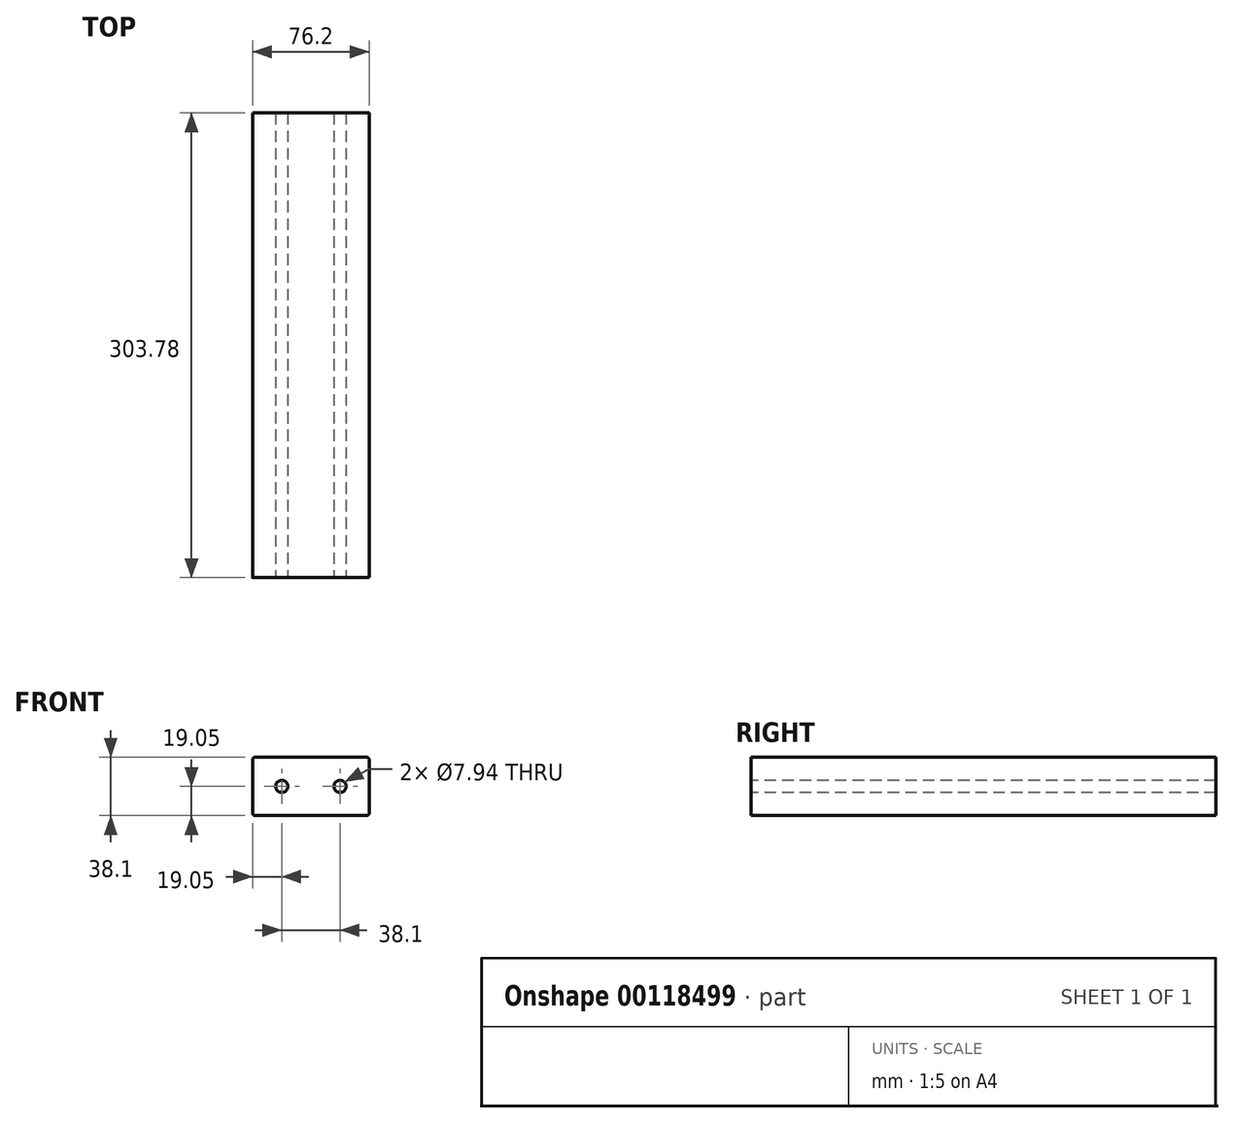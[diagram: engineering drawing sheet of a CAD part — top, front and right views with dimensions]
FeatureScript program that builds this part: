
annotation { "Feature Type Name" : "Feature", "Feature Type Description" : "" }
export const myFeature = defineFeature(function(context is Context, id is Id, definition is map)
    precondition{}
    {
        {
            var Q0;
            Q0=qCreatedBy(makeId("Front.planeOp"),FACE);
            var sketch = newSketch(context, id + "F0", { "sketchPlane" : qUnion([Q0])});
            skLineSegment(sketch, "E0.bottom", {"start": v(36.51, 19.05) * mm, "end": v(-36.51, 19.05) * mm});
            skLineSegment(sketch, "E0.top", {"start": v(36.51, -19.05) * mm, "end": v(-36.51, -19.05) * mm});
            skLineSegment(sketch, "E0.left", {"start": v(38.1, 17.46) * mm, "end": v(38.1, -17.46) * mm});
            skLineSegment(sketch, "E0.right", {"start": v(-38.1, 17.46) * mm, "end": v(-38.1, -17.46) * mm});
            skPoint(sketch, "E0.middle", {"position": v(0, 0) * mm});
            skPoint(sketch, "E1.visualSharp", {"position": v(38.1, 19.05) * mm});
            skArc(sketch, "E1.filletArc", {"start": v(38.1, 17.46) * mm, "mid": v(37.64, 18.59) * mm, "end": v(36.51, 19.05) * mm});
            skPoint(sketch, "E2.visualSharp", {"position": v(38.1, -19.05) * mm});
            skArc(sketch, "E2.filletArc", {"start": v(36.51, -19.05) * mm, "mid": v(37.64, -18.59) * mm, "end": v(38.1, -17.46) * mm});
            skPoint(sketch, "E3.visualSharp", {"position": v(-38.1, -19.05) * mm});
            skArc(sketch, "E3.filletArc", {"start": v(-38.1, -17.46) * mm, "mid": v(-37.64, -18.59) * mm, "end": v(-36.51, -19.05) * mm});
            skPoint(sketch, "E4.visualSharp", {"position": v(-38.1, 19.05) * mm});
            skArc(sketch, "E4.filletArc", {"start": v(-36.51, 19.05) * mm, "mid": v(-37.64, 18.59) * mm, "end": v(-38.1, 17.46) * mm});
            skSolve(sketch);
        }
        {
            var Q0;
            Q0=makeQuery(id+"F0.imprint","IMPRINT",FACE,{"disambiguationData":[TD([[makeQuery(id+"F0.imprint","IMPRINT",EDGE,{"derivedFrom":sQuery(id+"F0.wireOp",EDGE,"E0.bottom")}),1.0]])]});
            extrude(context, id + "F1", {"entities" : qUnion([Q0]), "depth" : 303.78 * mm, "symmetric" : true});
        }
        {
            var Q0;
            Q0=makeQuery(id+"F1.opExtrude","CAP_FACE",FACE,{"disambiguationData":[OSD([sQuery(id+"F0.wireOp",EDGE,"E0.bottom"),sQuery(id+"F0.wireOp",EDGE,"E0.top"),sQuery(id+"F0.wireOp",EDGE,"E0.left"),sQuery(id+"F0.wireOp",EDGE,"E0.right"),sQuery(id+"F0.wireOp",EDGE,"E1.filletArc"),sQuery(id+"F0.wireOp",EDGE,"E2.filletArc"),sQuery(id+"F0.wireOp",EDGE,"E3.filletArc"),sQuery(id+"F0.wireOp",EDGE,"E4.filletArc")])],"isStart":false});
            var sketch = newSketch(context, id + "F2", { "sketchPlane" : qUnion([Q0])});
            skLineSegment(sketch, "E5", {"start": v(0, 0) * mm, "end": v(19.05, 0) * mm});
            skCircle(sketch, "E6", {"center": v(19.05, 0) * mm, "radius": 3.97 * mm});
            skLineSegment(sketch, "E7", {"start": v(-19.05, 0) * mm, "end": v(0, 0) * mm});
            skCircle(sketch, "E8", {"center": v(-19.05, 0) * mm, "radius": 3.97 * mm});
            skSolve(sketch);
        }
        {
            var Q0;
            Q0=makeQuery(id+"F2.imprint","IMPRINT",FACE,{"disambiguationData":[TD([[makeQuery(id+"F2.imprint","IMPRINT",EDGE,{"derivedFrom":sQuery(id+"F2.wireOp",EDGE,"E6")}),1.0]])]});
            var Q1;
            Q1=makeQuery(id+"F2.imprint","IMPRINT",FACE,{"disambiguationData":[TD([[makeQuery(id+"F2.imprint","IMPRINT",EDGE,{"derivedFrom":sQuery(id+"F2.wireOp",EDGE,"E8")}),1.0]])]});
            var Q2;
            Q2=sQuery(id+"F2.wireOp",EDGE,"E6");
            extrude(context, id + "F3", {"entities" : qUnion([Q0, Q1]), "operationType" : NewBodyOperationType.REMOVE, "surfaceEntities" : qUnion([Q2]), "endBound" : BoundingType.THROUGH_ALL, "oppositeDirection" : true, "depth" : 25.4 * mm});
        }
    });
